# Revit family: IS_Ceraplus20_A6865_BIM_DE
name_source: partatom
category: Plumbing Fixtures
revit_build: Autodesk Revit 2015 (Build: 20140606_1530(x64)
units: mm (PartAtom-declared; Revit-internal decimal feet)

## types (1)
- A6865AA - CERAPLUS 2.0 SHR MXR B-IN CHR SL EASY-B.
    Accessories = www.idealspec.co.uk
    AreaUnits = millimeters
    Assembly Code = C1030200
    AssetType = Fixed
    BIMObjectName = ISI_IdealStandard_ShowerThermostaticValves_Ceraplus20_A6865
    BarCode = 4015413340533
    Brand = Ideal Standard
    Color = Chromium Plated
    ConnectionType = Plumbing
    Cost = 0 $
    Description = CERAPLUS 2.0 SHR MXR B-IN CHR SL EASY-B.
    DurationUnit = year
    Features = CERAPLUS 2.0 SHR MXR B-IN CHR SL EASY-B.
    Finish = Chromium Plated
    Help = www.idealstandard.de
    IfcExportAs = IfcValveType
    IfcExportType = SHOWER MIXERS
    InstallationInstructions = www.idealstandard.de
    LinearUnits = millimeters
    MainColor = Chromium Plated
    MaintenanceInformation = www.idealstandard.de
    Manufacturer = www.idealstandard.de
    ManufacturerURL = www.idealstandard.de
    Model = A6865AA
    ModelNumber = A6865AA
    ModelReference = CERAPLUS 2.0 SHR MXR B-IN CHR SL EASY-B.
    Name = ShowerThermostaticValves_Ceraplus20_A6865_ISI
    NettWeight = 0,00 KG
    NominalDepth = 180 mm
    NominalHeight = 215 mm
    NominalLength = 180 mm
    NominalWidth = 172 mm
    ProductInformation = www.idealstandard.de
    Shape = Sculptured
    Size = 215 x 180 x 172 mm
    Space = Internal
    SpareParts = www.idealstandard.de
    TestPressure = 10 bar
    URL = www.idealstandard.de
    Uniclass2015Code = Pr_40_20_87_80
    Uniclass2015Title = Shower thermostatic valves
    Uniclass2015Version = Products v1.1

## geometry (parser evidence)
native form markers: Blend x4
no freeform markers — native parametric forms only
